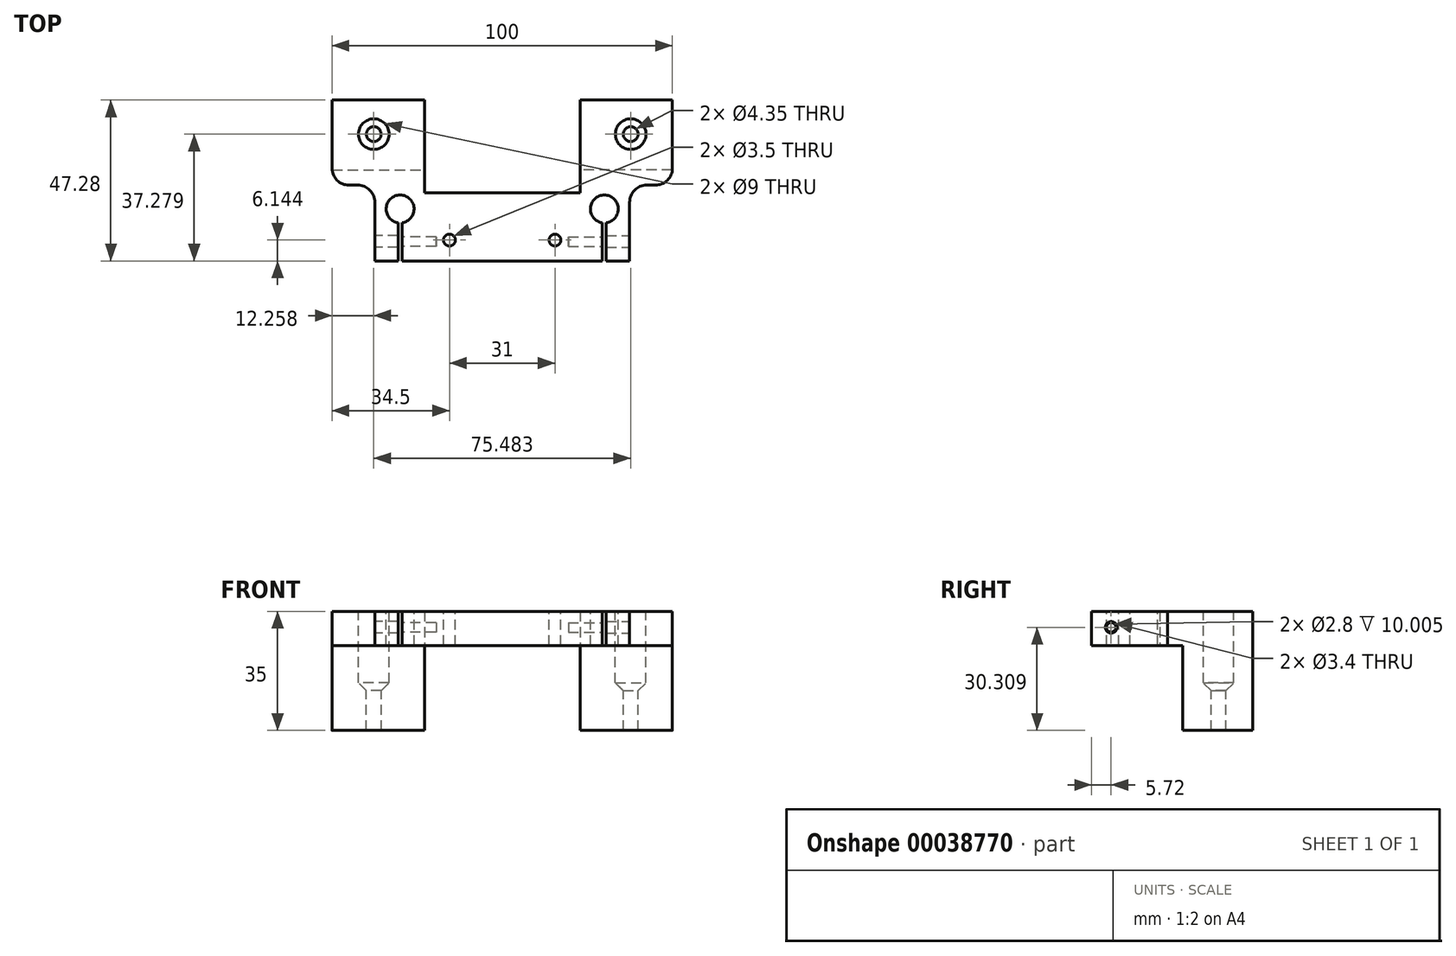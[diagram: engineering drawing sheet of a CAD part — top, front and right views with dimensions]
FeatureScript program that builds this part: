
annotation { "Feature Type Name" : "Feature", "Feature Type Description" : "" }
export const myFeature = defineFeature(function(context is Context, id is Id, definition is map)
    precondition{}
    {
        {
            var Q0;
            Q0=qCreatedBy(makeId("Top.planeOp"),FACE);
            var sketch = newSketch(context, id + "F0", { "sketchPlane" : qUnion([Q0])});
            skLineSegment(sketch, "E0", {"start": v(0, -13.82) * mm, "end": v(-37.44, -13.82) * mm});
            skLineSegment(sketch, "E1", {"start": v(-37.44, -13.82) * mm, "end": v(-37.44, 8.46) * mm});
            skLineSegment(sketch, "E2", {"start": v(-37.44, 8.46) * mm, "end": v(-50, 8.46) * mm});
            skLineSegment(sketch, "E3", {"start": v(-50, 8.46) * mm, "end": v(-50, 33.46) * mm});
            skLineSegment(sketch, "E4", {"start": v(-50, 33.46) * mm, "end": v(-22.87, 33.46) * mm});
            skLineSegment(sketch, "E5", {"start": v(-22.87, 33.46) * mm, "end": v(-22.87, 6.18) * mm});
            skLineSegment(sketch, "E6", {"start": v(-22.87, 6.18) * mm, "end": v(0, 6.18) * mm});
            skLineSegment(sketch, "E7", {"start": v(0, 6.18) * mm, "end": v(0, -13.82) * mm});
            skSolve(sketch);
        }
        {
            var Q0;
            Q0=qSketchRegion(id+"F0",true);
            extrude(context, id + "F1", {"entities" : qUnion([Q0]), "depth" : 10 * mm});
        }
        {
            var Q0;
            Q0=makeQuery(id+"F1.opExtrude","CAP_FACE",FACE,{"disambiguationData":[OSD([sQuery(id+"F0.wireOp",EDGE,"E0"),sQuery(id+"F0.wireOp",EDGE,"E1"),sQuery(id+"F0.wireOp",EDGE,"E2"),sQuery(id+"F0.wireOp",EDGE,"E3"),sQuery(id+"F0.wireOp",EDGE,"E4"),sQuery(id+"F0.wireOp",EDGE,"E5"),sQuery(id+"F0.wireOp",EDGE,"E6"),sQuery(id+"F0.wireOp",EDGE,"E7")])],"isStart":true});
            var sketch = newSketch(context, id + "F2", { "sketchPlane" : qUnion([Q0])});
            skLineSegment(sketch, "E8.bottom", {"start": v(-50, -33.46) * mm, "end": v(-22.87, -33.46) * mm});
            skLineSegment(sketch, "E8.top", {"start": v(-50, -12.92) * mm, "end": v(-22.87, -12.92) * mm});
            skLineSegment(sketch, "E8.left", {"start": v(-50, -33.46) * mm, "end": v(-50, -12.92) * mm});
            skLineSegment(sketch, "E8.right", {"start": v(-22.87, -33.46) * mm, "end": v(-22.87, -12.92) * mm});
            skSolve(sketch);
        }
        {
            var Q0;
            Q0=qSketchRegion(id+"F2",true);
            extrude(context, id + "F3", {"entities" : qUnion([Q0]), "operationType" : NewBodyOperationType.ADD, "depth" : 25 * mm});
        }
        {
            var Q0;
            {var subQ0=makeQuery(id+"F1.opExtrude","CAP_FACE",FACE,{"disambiguationData":[OSD([sQuery(id+"F0.wireOp",EDGE,"E0"),sQuery(id+"F0.wireOp",EDGE,"fd64a43a-5635-4f94-a977-4dd36923accb"),sQuery(id+"F0.wireOp",EDGE,"1334f7d4-4c90-4769-8fa3-fe5f576fb005"),sQuery(id+"F0.wireOp",EDGE,"E1"),sQuery(id+"F0.wireOp",EDGE,"E2"),sQuery(id+"F0.wireOp",EDGE,"E3"),sQuery(id+"F0.wireOp",EDGE,"E4"),sQuery(id+"F0.wireOp",EDGE,"E5"),sQuery(id+"F0.wireOp",EDGE,"E6"),sQuery(id+"F0.wireOp",EDGE,"E7")])],"isStart":false});Q0=makeQuery(id+"F15.boolean.opBoolean","MERGE",FACE,{"derivedFrom":[subQ0,makeQuery(id+"F15.opPattern","COPY",FACE,{"derivedFrom":subQ0,"instanceName":"1"})]});}
            var sketch = newSketch(context, id + "F4", { "sketchPlane" : qUnion([Q0])});
            skCircle(sketch, "E9", {"center": v(-30, 1.46) * mm, "radius": 4.1 * mm});
            skCircle(sketch, "E10", {"center": v(-37.74, 23.46) * mm, "radius": 2.17 * mm});
            skLineSegment(sketch, "E11", {"start": v(-30, 1.46) * mm, "end": v(-30, -13.82) * mm, "construction": true});
            skLineSegment(sketch, "E12.bottom", {"start": v(-30.55, -1.63) * mm, "end": v(-29.45, -1.63) * mm});
            skLineSegment(sketch, "E12.top", {"start": v(-30.55, -14.74) * mm, "end": v(-29.45, -14.74) * mm});
            skLineSegment(sketch, "E12.left", {"start": v(-30.55, -1.63) * mm, "end": v(-30.55, -14.74) * mm});
            skLineSegment(sketch, "E12.right", {"start": v(-29.45, -1.63) * mm, "end": v(-29.45, -14.74) * mm});
            skPoint(sketch, "E13", {"position": v(-30, -1.63) * mm});
            skCircle(sketch, "E14", {"center": v(-37.74, 23.46) * mm, "radius": 4.5 * mm});
            skSolve(sketch);
        }
        {
            var Q0;
            {var subQ3=sQuery(id+"F4.wireOp",EDGE,"E12.bottom");Q0=makeQuery(id+"F4.imprint","IMPRINT",FACE,{"disambiguationData":[TD([[makeQuery(id+"F4.imprint","IMPRINT",EDGE,{"derivedFrom":subQ3}),1.0]])]});}
            var Q1;
            {var subQ5=sQuery(id+"F4.wireOp",EDGE,"E12.top");Q1=makeQuery(id+"F4.imprint","IMPRINT",FACE,{"disambiguationData":[TD([[makeQuery(id+"F4.imprint","IMPRINT",EDGE,{"derivedFrom":subQ5}),1.0]])]});}
            var Q2;
            {var subQ3=sQuery(id+"F4.wireOp",EDGE,"E12.left");var subQ5=sQuery(id+"F4.wireOp",EDGE,"E9");var subQ7=makeQuery(id+"F4.imprint","INTERSECT",VERTEX,{"derivedFrom":[subQ5,subQ3]});Q2=makeQuery(id+"F4.imprint","IMPRINT",FACE,{"disambiguationData":[TD([[makeQuery(id+"F4.imprint","IMPRINT",EDGE,{"disambiguationData":[TD([[subQ7,-1.0]])],"derivedFrom":subQ5}),-1.0]])]});}
            var Q3;
            {var subQ3=sQuery(id+"F4.wireOp",EDGE,"E12.bottom");Q3=makeQuery(id+"F4.imprint","IMPRINT",FACE,{"disambiguationData":[TD([[makeQuery(id+"F4.imprint","IMPRINT",EDGE,{"derivedFrom":subQ3}),-1.0]])]});}
            var Q4;
            Q4=makeQuery(id+"F4.imprint","IMPRINT",FACE,{"disambiguationData":[TD([[makeQuery(id+"F4.imprint","IMPRINT",EDGE,{"derivedFrom":sQuery(id+"F4.wireOp",EDGE,"E10")}),1.0]])]});
            extrude(context, id + "F5", {"entities" : qUnion([Q0, Q1, Q2, Q3, Q4]), "operationType" : NewBodyOperationType.REMOVE, "endBound" : BoundingType.THROUGH_ALL, "oppositeDirection" : true, "depth" : 25 * mm});
        }
        {
            var Q0;
            Q0=makeQuery(id+"F1.opExtrude","SWEPT_EDGE",EDGE,{"disambiguationData":[OSD([sQuery(id+"F0.wireOp",EDGE,"E2"),sQuery(id+"F0.wireOp",EDGE,"E3")])]});
            fillet(context, id + "F6", {"entities" : qUnion([Q0]), "radius" : 5 * mm, "tangentPropagation" : true, "allowEdgeOverflow" : false});
        }
        {
            var Q0;
            Q0=makeQuery(id+"F1.opExtrude","SWEPT_EDGE",EDGE,{"disambiguationData":[OSD([sQuery(id+"F0.wireOp",EDGE,"E1"),sQuery(id+"F0.wireOp",EDGE,"E2")])]});
            fillet(context, id + "F7", {"entities" : qUnion([Q0]), "radius" : 5 * mm, "tangentPropagation" : true, "allowEdgeOverflow" : false});
        }
        {
            var Q0;
            Q0=makeQuery(id+"F1.opExtrude","SWEPT_FACE",FACE,{"disambiguationData":[OSD([sQuery(id+"F0.wireOp",EDGE,"E1")])]});
            var sketch = newSketch(context, id + "F8", { "sketchPlane" : qUnion([Q0])});
            skCircle(sketch, "E15", {"center": v(8.1, 5.3) * mm, "radius": 1.7 * mm});
            skCircle(sketch, "E16", {"center": v(8.1, 5.3) * mm, "radius": 1.4 * mm});
            skSolve(sketch);
        }
        {
            var Q0;
            Q0=makeQuery(id+"F8.imprint","IMPRINT",FACE,{"disambiguationData":[TD([[makeQuery(id+"F8.imprint","IMPRINT",EDGE,{"derivedFrom":sQuery(id+"F8.wireOp",EDGE,"E16")}),1.0]])]});
            extrude(context, id + "F9", {"entities" : qUnion([Q0]), "operationType" : NewBodyOperationType.REMOVE, "oppositeDirection" : true, "depth" : 18 * mm});
        }
        {
            var Q0;
            Q0=makeQuery(id+"F8.imprint","IMPRINT",FACE,{"disambiguationData":[TD([[makeQuery(id+"F8.imprint","IMPRINT",EDGE,{"derivedFrom":sQuery(id+"F8.wireOp",EDGE,"E16")}),1.0]])]});
            var Q1;
            Q1=makeQuery(id+"F8.imprint","IMPRINT",FACE,{"disambiguationData":[TD([[makeQuery(id+"F8.imprint","IMPRINT",EDGE,{"derivedFrom":sQuery(id+"F8.wireOp",EDGE,"E15")}),1.0]])]});
            extrude(context, id + "F10", {"entities" : qUnion([Q0, Q1]), "operationType" : NewBodyOperationType.REMOVE, "endBound" : BoundingType.UP_TO_NEXT, "oppositeDirection" : true, "depth" : 25 * mm});
        }
        {
            var Q0;
            Q0=makeQuery(id+"F1.opExtrude","CAP_FACE",FACE,{"disambiguationData":[OSD([sQuery(id+"F0.wireOp",EDGE,"E0"),sQuery(id+"F0.wireOp",EDGE,"E1"),sQuery(id+"F0.wireOp",EDGE,"E2"),sQuery(id+"F0.wireOp",EDGE,"E3"),sQuery(id+"F0.wireOp",EDGE,"E4"),sQuery(id+"F0.wireOp",EDGE,"E5"),sQuery(id+"F0.wireOp",EDGE,"E6"),sQuery(id+"F0.wireOp",EDGE,"E7")])],"isStart":false});
            var sketch = newSketch(context, id + "F11", { "sketchPlane" : qUnion([Q0])});
            skCircle(sketch, "E17", {"center": v(-15.5, -7.68) * mm, "radius": 1.75 * mm});
            skPoint(sketch, "E17.centerSnap0", {"position": v(0, -7.68) * mm});
            skSolve(sketch);
        }
        {
            var Q0;
            Q0=makeQuery(id+"F11.imprint","IMPRINT",FACE,{"disambiguationData":[TD([[makeQuery(id+"F11.imprint","IMPRINT",EDGE,{"derivedFrom":sQuery(id+"F11.wireOp",EDGE,"E17")}),1.0]])]});
            extrude(context, id + "F12", {"entities" : qUnion([Q0]), "operationType" : NewBodyOperationType.REMOVE, "oppositeDirection" : true, "depth" : 25 * mm});
        }
        {
            var Q0;
            Q0=makeQuery(id+"F4.imprint","IMPRINT",FACE,{"disambiguationData":[TD([[makeQuery(id+"F4.imprint","IMPRINT",EDGE,{"derivedFrom":sQuery(id+"F4.wireOp",EDGE,"E10")}),-1.0]])]});
            extrude(context, id + "F13", {"entities" : qUnion([Q0]), "operationType" : NewBodyOperationType.REMOVE, "oppositeDirection" : true, "depth" : 25 * mm});
        }
        {
            var Q0;
            Q0=makeQuery(id+"F13.boolean.opBoolean","COPY",EDGE,{"derivedFrom":makeQuery(id+"F13.opExtrude","CAP_EDGE",EDGE,{"disambiguationData":[OSD([sQuery(id+"F4.wireOp",EDGE,"E14")])],"isStart":false})});
            chamfer(context, id + "F14", {"entities" : qUnion([Q0]), "width" : 4 * mm, "tangentPropagation" : true});
        }
        {
            var Q0;
            Q0=makeQuery(id+"F1.opExtrude","SWEPT_BODY",BODY,{"disambiguationData":[OSD([sQuery(id+"F0.wireOp",EDGE,"E0"),sQuery(id+"F0.wireOp",EDGE,"fd64a43a-5635-4f94-a977-4dd36923accb"),sQuery(id+"F0.wireOp",EDGE,"1334f7d4-4c90-4769-8fa3-fe5f576fb005"),sQuery(id+"F0.wireOp",EDGE,"E1"),sQuery(id+"F0.wireOp",EDGE,"E2"),sQuery(id+"F0.wireOp",EDGE,"E3"),sQuery(id+"F0.wireOp",EDGE,"E4"),sQuery(id+"F0.wireOp",EDGE,"E5"),sQuery(id+"F0.wireOp",EDGE,"E6"),sQuery(id+"F0.wireOp",EDGE,"E7")])]});
            var Q1;
            Q1=qCreatedBy(makeId("Right.planeOp"),FACE);
            mirror(context, id + "F15", {"operationType" : NewBodyOperationType.ADD, "entities" : qUnion([Q0]), "mirrorPlane" : qUnion([Q1])});
        }
    });
